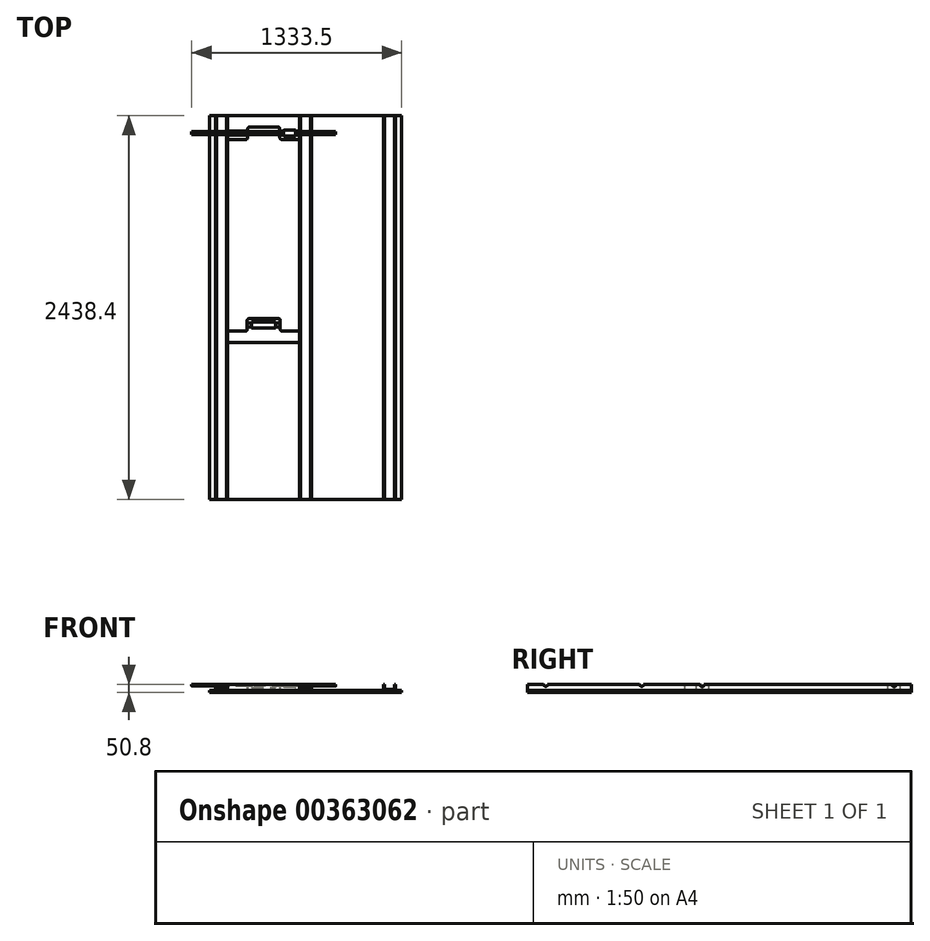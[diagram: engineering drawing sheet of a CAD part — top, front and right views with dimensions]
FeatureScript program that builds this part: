
annotation { "Feature Type Name" : "Feature", "Feature Type Description" : "" }
export const myFeature = defineFeature(function(context is Context, id is Id, definition is map)
    precondition{}
    {
        {
            var Q0;
            Q0=qCreatedBy(makeId("Top.planeOp"),FACE);
            var sketch = newSketch(context, id + "F0", { "sketchPlane" : qUnion([Q0])});
            skLineSegment(sketch, "E0.bottom", {"start": v(-609.6, 1219.2) * mm, "end": v(609.6, 1219.2) * mm});
            skLineSegment(sketch, "E0.top", {"start": v(-609.6, -1219.2) * mm, "end": v(609.6, -1219.2) * mm});
            skLineSegment(sketch, "E0.left", {"start": v(-609.6, 1219.2) * mm, "end": v(-609.6, -1219.2) * mm});
            skLineSegment(sketch, "E0.right", {"start": v(609.6, 1219.2) * mm, "end": v(609.6, -1219.2) * mm});
            skPoint(sketch, "E0.middle", {"position": v(0, 0) * mm});
            skSolve(sketch);
        }
        {
            var Q0;
            Q0=qSketchRegion(id+"F0",true);
            extrude(context, id + "F1", {"entities" : qUnion([Q0]), "depth" : 12.7 * mm});
        }
        {
            var Q0;
            Q0=qCreatedBy(makeId("Front.planeOp"),FACE);
            var sketch = newSketch(context, id + "F2", { "sketchPlane" : qUnion([Q0])});
            skLineSegment(sketch, "E1.bottom", {"start": v(38.1, 88.9) * mm, "end": v(-38.1, 88.9) * mm});
            skLineSegment(sketch, "E1.top", {"start": v(38.1, 12.7) * mm, "end": v(-38.1, 12.7) * mm});
            skLineSegment(sketch, "E1.left", {"start": v(38.1, 88.9) * mm, "end": v(38.1, 12.7) * mm});
            skLineSegment(sketch, "E1.right", {"start": v(-38.1, 88.9) * mm, "end": v(-38.1, 12.7) * mm});
            skPoint(sketch, "E1.middle", {"position": v(0, 50.8) * mm});
            skLineSegment(sketch, "E2.bottom", {"start": v(31.75, 82.55) * mm, "end": v(-31.75, 82.55) * mm});
            skLineSegment(sketch, "E2.top", {"start": v(31.75, 19.05) * mm, "end": v(-31.75, 19.05) * mm});
            skLineSegment(sketch, "E2.left", {"start": v(31.75, 82.55) * mm, "end": v(31.75, 19.05) * mm});
            skLineSegment(sketch, "E2.right", {"start": v(-31.75, 82.55) * mm, "end": v(-31.75, 19.05) * mm});
            skLineSegment(sketch, "E3.bottom", {"start": v(-495.3, 88.9) * mm, "end": v(-571.5, 88.9) * mm});
            skLineSegment(sketch, "E3.top", {"start": v(-495.3, 12.7) * mm, "end": v(-571.5, 12.7) * mm});
            skLineSegment(sketch, "E3.left", {"start": v(-495.3, 88.9) * mm, "end": v(-495.3, 12.7) * mm});
            skLineSegment(sketch, "E3.right", {"start": v(-571.5, 88.9) * mm, "end": v(-571.5, 12.7) * mm});
            skPoint(sketch, "E3.middle", {"position": v(-533.4, 50.8) * mm});
            skLineSegment(sketch, "E4.bottom", {"start": v(571.5, 88.9) * mm, "end": v(495.3, 88.9) * mm});
            skLineSegment(sketch, "E4.top", {"start": v(571.5, 12.7) * mm, "end": v(495.3, 12.7) * mm});
            skLineSegment(sketch, "E4.left", {"start": v(571.5, 88.9) * mm, "end": v(571.5, 12.7) * mm});
            skLineSegment(sketch, "E4.right", {"start": v(495.3, 88.9) * mm, "end": v(495.3, 12.7) * mm});
            skPoint(sketch, "E4.middle", {"position": v(533.4, 50.8) * mm});
            skLineSegment(sketch, "E5.bottom", {"start": v(-565.15, 82.55) * mm, "end": v(-501.65, 82.55) * mm});
            skLineSegment(sketch, "E5.top", {"start": v(-565.15, 19.05) * mm, "end": v(-501.65, 19.05) * mm});
            skLineSegment(sketch, "E5.left", {"start": v(-565.15, 82.55) * mm, "end": v(-565.15, 19.05) * mm});
            skLineSegment(sketch, "E5.right", {"start": v(-501.65, 82.55) * mm, "end": v(-501.65, 19.05) * mm});
            skLineSegment(sketch, "E6.bottom", {"start": v(501.65, 82.55) * mm, "end": v(565.15, 82.55) * mm});
            skLineSegment(sketch, "E6.top", {"start": v(501.65, 19.05) * mm, "end": v(565.15, 19.05) * mm});
            skLineSegment(sketch, "E6.left", {"start": v(501.65, 82.55) * mm, "end": v(501.65, 19.05) * mm});
            skLineSegment(sketch, "E6.right", {"start": v(565.15, 82.55) * mm, "end": v(565.15, 19.05) * mm});
            skSolve(sketch);
        }
        {
            var Q0;
            Q0=qSketchRegion(id+"F2",true);
            extrude(context, id + "F3", {"entities" : qUnion([Q0]), "endBound" : BoundingType.SYMMETRIC, "depth" : 2438.4 * mm});
        }
        {
            var Q0;
            Q0=makeQuery(id+"F1.opExtrude","CAP_FACE",FACE,{"disambiguationData":[OSD([sQuery(id+"F0.wireOp",EDGE,"E0.bottom"),sQuery(id+"F0.wireOp",EDGE,"E0.top"),sQuery(id+"F0.wireOp",EDGE,"E0.left"),sQuery(id+"F0.wireOp",EDGE,"E0.right")])],"isStart":false});
            var sketch = newSketch(context, id + "F4", { "sketchPlane" : qUnion([Q0])});
            skLineSegment(sketch, "E7.0", {"start": v(-495.3, -1219.2) * mm, "end": v(-495.3, 1219.2) * mm});
            skLineSegment(sketch, "E8.0", {"start": v(-38.1, -1219.2) * mm, "end": v(-38.1, 1219.2) * mm});
            skLineSegment(sketch, "E9.0", {"start": v(38.1, -1219.2) * mm, "end": v(38.1, 1219.2) * mm});
            skLineSegment(sketch, "E10.0", {"start": v(495.3, -1219.2) * mm, "end": v(495.3, 1219.2) * mm});
            skLineSegment(sketch, "E11", {"start": v(-495.3, 1066.8) * mm, "end": v(-368.3, 1066.8) * mm});
            skLineSegment(sketch, "E12", {"start": v(-368.3, 1066.8) * mm, "end": v(-368.3, 1146.18) * mm});
            skLineSegment(sketch, "E13", {"start": v(-368.3, 1146.18) * mm, "end": v(-165.1, 1146.18) * mm});
            skLineSegment(sketch, "E14", {"start": v(-165.1, 1146.18) * mm, "end": v(-165.1, 1066.8) * mm});
            skLineSegment(sketch, "E15", {"start": v(-165.1, 1066.8) * mm, "end": v(-38.1, 1066.8) * mm});
            skLineSegment(sketch, "E16", {"start": v(-495.3, 1219.2) * mm, "end": v(-38.1, 1219.2) * mm});
            skLineSegment(sketch, "E17", {"start": v(-495.3, -1219.2) * mm, "end": v(-38.1, -1219.2) * mm});
            skLineSegment(sketch, "E18", {"start": v(0, 1288.87) * mm, "end": v(0, -1353.9) * mm, "construction": true});
            skPoint(sketch, "E18.startSnap0", {"position": v(0, 1219.2) * mm});
            skLineSegment(sketch, "E19", {"start": v(-495.3, -149.23) * mm, "end": v(-371.48, -149.23) * mm});
            skLineSegment(sketch, "E20", {"start": v(-371.48, -149.23) * mm, "end": v(-371.48, -69.85) * mm});
            skLineSegment(sketch, "E21", {"start": v(-371.48, -69.85) * mm, "end": v(-161.93, -69.85) * mm});
            skLineSegment(sketch, "E22", {"start": v(-161.93, -69.85) * mm, "end": v(-161.93, -149.23) * mm});
            skLineSegment(sketch, "E23", {"start": v(-161.93, -149.23) * mm, "end": v(-38.1, -149.23) * mm});
            skLineSegment(sketch, "E24", {"start": v(-38.1, -222.25) * mm, "end": v(-495.3, -222.25) * mm});
            skLineSegment(sketch, "E25", {"start": v(-368.3, 1108.07) * mm, "end": v(-165.1, 1108.07) * mm, "construction": true});
            skLineSegment(sketch, "E26", {"start": v(-371.48, -111.13) * mm, "end": v(-161.93, -111.13) * mm, "construction": true});
            skSolve(sketch);
        }
        {
            var Q0;
            {var subQ0=sQuery(id+"F4.wireOp",EDGE,"E11");Q0=makeQuery(id+"F4.imprint","IMPRINT",FACE,{"disambiguationData":[TD([[makeQuery(id+"F4.imprint","IMPRINT",EDGE,{"derivedFrom":subQ0}),1.0]])]});}
            var Q1;
            {var subQ0=sQuery(id+"F4.wireOp",EDGE,"E19");Q1=makeQuery(id+"F4.imprint","IMPRINT",FACE,{"disambiguationData":[TD([[makeQuery(id+"F4.imprint","IMPRINT",EDGE,{"derivedFrom":subQ0}),-1.0]])]});}
            var Q2;
            Q2=makeQuery(id+"F3.opExtrude","SWEPT_FACE",FACE,{"disambiguationData":[OSD([sQuery(id+"F2.wireOp",EDGE,"E3.bottom")])]});
            extrude(context, id + "F5", {"entities" : qUnion([Q0, Q1]), "endBound" : BoundingType.UP_TO_SURFACE, "endBoundEntityFace" : qUnion([Q2]), "depth" : 25.4 * mm});
        }
        {
            var Q0;
            Q0=qCreatedBy(makeId("Right.planeOp"),FACE);
            var sketch = newSketch(context, id + "F6", { "sketchPlane" : qUnion([Q0])});
            skCircle(sketch, "E27", {"center": v(1108.08, 50.8) * mm, "radius": 12.7 * mm});
            skCircle(sketch, "E28", {"center": v(-111.12, 50.8) * mm, "radius": 12.7 * mm});
            skCircle(sketch, "E29", {"center": v(-495.3, 50.8) * mm, "radius": 12.7 * mm});
            skCircle(sketch, "E30", {"center": v(-1104.9, 50.8) * mm, "radius": 12.7 * mm});
            skSolve(sketch);
        }
        {
            var Q0;
            Q0=qSketchRegion(id+"F6",true);
            extrude(context, id + "F7", {"entities" : qUnion([Q0]), "operationType" : NewBodyOperationType.REMOVE, "endBound" : BoundingType.SYMMETRIC, "depth" : 1219.2 * mm});
        }
        {
            var Q0;
            Q0=makeQuery(id+"F5.opExtrude","SWEPT_EDGE",EDGE,{"disambiguationData":[OSD([sQuery(id+"F4.wireOp",EDGE,"E13"),sQuery(id+"F4.wireOp",EDGE,"E14")])]});
            var Q1;
            Q1=makeQuery(id+"F5.opExtrude","SWEPT_EDGE",EDGE,{"disambiguationData":[OSD([sQuery(id+"F4.wireOp",EDGE,"E12"),sQuery(id+"F4.wireOp",EDGE,"E13")])]});
            var Q2;
            Q2=makeQuery(id+"F5.opExtrude","SWEPT_EDGE",EDGE,{"disambiguationData":[OSD([sQuery(id+"F4.wireOp",EDGE,"E19"),sQuery(id+"F4.wireOp",EDGE,"E20")])]});
            var Q3;
            Q3=makeQuery(id+"F5.opExtrude","SWEPT_EDGE",EDGE,{"disambiguationData":[OSD([sQuery(id+"F4.wireOp",EDGE,"E22"),sQuery(id+"F4.wireOp",EDGE,"E23")])]});
            fillet(context, id + "F8", {"entities" : qUnion([Q0, Q1, Q2, Q3]), "radius" : 9.52 * mm, "tangentPropagation" : true, "allowEdgeOverflow" : false});
        }
        {
            var Q0;
            Q0=makeQuery(id+"F5.opExtrude","SWEPT_EDGE",EDGE,{"disambiguationData":[OSD([sQuery(id+"F4.wireOp",EDGE,"E21"),sQuery(id+"F4.wireOp",EDGE,"E22")])]});
            var Q1;
            Q1=makeQuery(id+"F5.opExtrude","SWEPT_EDGE",EDGE,{"disambiguationData":[OSD([sQuery(id+"F4.wireOp",EDGE,"E20"),sQuery(id+"F4.wireOp",EDGE,"E21")])]});
            var Q2;
            Q2=makeQuery(id+"F5.opExtrude","SWEPT_EDGE",EDGE,{"disambiguationData":[OSD([sQuery(id+"F4.wireOp",EDGE,"E14"),sQuery(id+"F4.wireOp",EDGE,"E15")])]});
            var Q3;
            Q3=makeQuery(id+"F5.opExtrude","SWEPT_EDGE",EDGE,{"disambiguationData":[OSD([sQuery(id+"F4.wireOp",EDGE,"E11"),sQuery(id+"F4.wireOp",EDGE,"E12")])]});
            fillet(context, id + "F9", {"entities" : qUnion([Q0, Q1, Q2, Q3]), "radius" : 12.7 * mm, "tangentPropagation" : true, "allowEdgeOverflow" : false});
        }
        {
            var Q0;
            Q0=makeQuery(id+"F3.opExtrude","SWEPT_FACE",FACE,{"disambiguationData":[OSD([sQuery(id+"F2.wireOp",EDGE,"E3.left")])]});
            cPlane(context, id + "F10", {"entities" : qUnion([Q0]), "cplaneType" : CPlaneType.OFFSET, "offset" : 228.6 * mm, "width" : 152.4 * mm, "height" : 152.4 * mm});
        }
        {
            var Q0;
            Q0=qCreatedBy(id+"F10.planeOp",FACE);
            var sketch = newSketch(context, id + "F11", { "sketchPlane" : qUnion([Q0])});
            skCircle(sketch, "E31.0", {"center": v(1108.08, 50.8) * mm, "radius": 12.7 * mm});
            skCircle(sketch, "E32", {"center": v(1108.08, 50.8) * mm, "radius": 10.67 * mm});
            skSolve(sketch);
        }
        {
            var Q0;
            Q0=makeQuery(id+"F11.imprint","IMPRINT",FACE,{"disambiguationData":[TD([[makeQuery(id+"F11.imprint","IMPRINT",EDGE,{"derivedFrom":sQuery(id+"F11.wireOp",EDGE,"E32")}),1.0]])]});
            extrude(context, id + "F12", {"entities" : qUnion([Q0]), "endBound" : BoundingType.SYMMETRIC, "depth" : 914.4 * mm});
        }
        {
            var Q0;
            Q0=makeQuery(id+"F1.opExtrude","CAP_FACE",FACE,{"disambiguationData":[OSD([sQuery(id+"F0.wireOp",EDGE,"E0.bottom"),sQuery(id+"F0.wireOp",EDGE,"E0.top"),sQuery(id+"F0.wireOp",EDGE,"E0.left"),sQuery(id+"F0.wireOp",EDGE,"E0.right")])],"isStart":false});
            cPlane(context, id + "F13", {"entities" : qUnion([Q0]), "cplaneType" : CPlaneType.OFFSET, "offset" : 38.1 * mm, "width" : 152.4 * mm, "height" : 152.4 * mm});
        }
        {
            var Q0;
            Q0=qCreatedBy(id+"F13.planeOp",FACE);
            var sketch = newSketch(context, id + "F14", { "sketchPlane" : qUnion([Q0])});
            skLineSegment(sketch, "E33.bottom", {"start": v(725.78, 1411.34) * mm, "end": v(-725.78, 1411.34) * mm});
            skLineSegment(sketch, "E33.top", {"start": v(725.78, -1411.34) * mm, "end": v(-725.78, -1411.34) * mm});
            skLineSegment(sketch, "E33.left", {"start": v(725.78, 1411.34) * mm, "end": v(725.78, -1411.34) * mm});
            skLineSegment(sketch, "E33.right", {"start": v(-725.78, 1411.34) * mm, "end": v(-725.78, -1411.34) * mm});
            skPoint(sketch, "E33.middle", {"position": v(0, 0) * mm});
            skSolve(sketch);
        }
        {
            var Q0;
            Q0=qSketchRegion(id+"F14",true);
            extrude(context, id + "F15", {"entities" : qUnion([Q0]), "operationType" : NewBodyOperationType.REMOVE, "endBound" : BoundingType.THROUGH_ALL, "depth" : 25.4 * mm, "offsetDistance" : 25.4 * mm});
        }
        {
            var Q0;
            Q0=qCreatedBy(id+"F10.planeOp",FACE);
            cPlane(context, id + "F16", {"entities" : qUnion([Q0]), "cplaneType" : CPlaneType.OFFSET, "offset" : 165.1 * mm, "width" : 152.4 * mm, "height" : 152.4 * mm});
        }
        {
            var Q0;
            Q0=qCreatedBy(id+"F16.planeOp",FACE);
            var sketch = newSketch(context, id + "F17", { "sketchPlane" : qUnion([Q0])});
            skCircle(sketch, "E34", {"center": v(1108.08, 50.8) * mm, "radius": 19.05 * mm});
            skSolve(sketch);
        }
        {
            var Q0;
            Q0=qSketchRegion(id+"F17",true);
            extrude(context, id + "F18", {"entities" : qUnion([Q0]), "operationType" : NewBodyOperationType.REMOVE, "endBound" : BoundingType.SYMMETRIC, "depth" : 76.2 * mm, "offsetDistance" : 25.4 * mm});
        }
        {
            var Q0;
            Q0=makeQuery(id+"F18.boolean.opBoolean","COPY",EDGE,{"derivedFrom":makeQuery(id+"F18.opExtrude","CAP_EDGE",EDGE,{"disambiguationData":[OSD([sQuery(id+"F17.wireOp",EDGE,"E34")])],"isStart":true})});
            var Q1;
            Q1=makeQuery(id+"F18.boolean.opBoolean","COPY",EDGE,{"derivedFrom":makeQuery(id+"F18.opExtrude","CAP_EDGE",EDGE,{"disambiguationData":[OSD([sQuery(id+"F17.wireOp",EDGE,"E34")])],"isStart":false})});
            fillet(context, id + "F19", {"entities" : qUnion([Q0, Q1]), "radius" : 3.17 * mm, "tangentPropagation" : true, "allowEdgeOverflow" : false});
        }
        {
            var Q0;
            Q0=qCreatedBy(id+"F10.planeOp",FACE);
            var sketch = newSketch(context, id + "F20", { "sketchPlane" : qUnion([Q0])});
            skCircle(sketch, "E35", {"center": v(-111.12, 50.8) * mm, "radius": 19.05 * mm});
            skSolve(sketch);
        }
        {
            var Q0;
            Q0 = qSketchRegion(id + "F20", true);
            extrude(context, id + "F21", {"entities" : qUnion([Q0]), "operationType" : NewBodyOperationType.REMOVE, "endBound" : BoundingType.SYMMETRIC, "oppositeDirection" : true, "depth" : 152.4 * mm, "offsetDistance" : 25.4 * mm});
        }
    });
